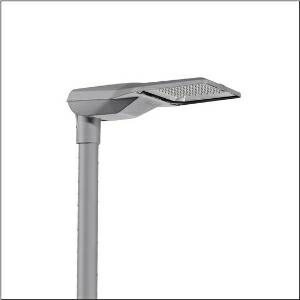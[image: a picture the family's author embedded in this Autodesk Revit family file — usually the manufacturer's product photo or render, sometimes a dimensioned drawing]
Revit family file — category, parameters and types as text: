
# Revit family: streetlight_sl_21_iq_midi___pl52_5xe3h41g08mb_9f92
name_source: partatom
category: Lighting Fixtures
units: mm (PartAtom-declared; Revit-internal decimal feet)

## family parameters
Cut with Voids When Loaded = No
Host = Face
Light Source = No
Part Type = Normal
Room Calculation Point = No
Round Connector Dimension = Use Diameter
Shared = No

## types (1)
- --- (1 x LED, 20000 lm, 146.7 W, 4000K)
    Apparent Load = 147 VA
    CIE Flux Codes = 27 59 98 100 100
    Color Rendering = 70
    Color Temperature = 4000K
    Default Elevation = 1800 mm
    Description = Streetlight SL 21 iQ midi, mast luminaire, primary light control with lens, of PMMA, primary optical cover: cover, of toughened safety glass, transparent, light distribution: PL52, light emission: direct distribution, primary light characteristic: asymmetric, installation type: post-top, side-entry, LED, High Power LED, rated luminous flux: 20.000lm, luminous efficacy: 136lm/W, light colour: 740, colour temperature: 4000K, control gear: iQ Street-Remote, control: Street-Remote, Auto-Match, Temp-Guard, Lumen-Switch, Night-Set, Smart-Wire, Light-Fading, Desk-Remote (wireless, voltage-free reading and setting of iQ features in the workshop via application-optimized NFC function/RFID function), optimised constant luminous flux control (CLO 2.0), pre-setting: linear dimming characteristic, mains connection: 230..240V, AC, 50/60Hz, start of lifetime: 147W, end of service life: 161W, reduction: 62W, luminaire housing, of diecast aluminium, powder-coated, Siteco® metallic grey (DB 702S), corrosivity category C5 mid according to DIN EN ISO 12944, please order mast flange separately, inclination adjustable: 0°, 5°, 10°, 15°, sealing non-destructively replaceable, multi-level sealing system, length: 644mm, width: 335mm, height: 110mm, mast flange for spigot size: 42mm (side-entry): 5XC10008XM4, 60/48mm (side-entry/post-top): 5XC10108XM2, 76/60mm (side-entry/post-top): 5XC10108XM1, mounting height: 4..8m, protection rating (complete): IP66, insulation class (complete): insulation class II (safety insulation), certification: CE, ENEC, ENEC+, VDE, impact resistance: IK10, permissible operating ambient temperature for outdoor applications: -40..+50°C, standard-compliant lighting for roads and squares, packaging unit: 1 piece

Light Distribution: PL52
    Height = 111 mm
    Lamp = 1 x LED
    Lamp Light Flux = 20000 lm
    Lamp Power = 146.7 W
    Lamp count = 1
    Length = 644 mm
    Luminous efficacy = 136 lm/W
    Manufacturer = Siteco
    ModVariant = No
    Model = 5XE3H41G08MB
    Number of Poles = 1
    OnlyDefault = Yes
    Power Factor = 1
    Product Name = Streetlight SL 21 iQ midi | PL52
    Product group = mast luminaire | pylon top
    ProductGroupID = 6100
    Protection Class = Protection class II
    Protection Degree = IP 66
    RLX_Detail_Level = 1
    RLX_Emergency_Light_Flux = 0 lm
    RLX_Emergency_Type = 0
    RLX_Emergency_Type_DB = No
    RlxData = <blob elided: 36625 chars, md5=75058d87>
    Socket = socket
    Standby Power = 0 W
    System Light Flux = 20000 lm
    System Power = 147 W
    Type Comments = factory setting: luminous flux: 100 % | dim-lin: 254 | 753 mA
    Type Image = l_1004298.jpg
    URL = http://relux.com
    VarID = @adj_212003
    Voltage = 0 V
    Weight = 0.00 kg
    Width = 336 mm

## geometry (parser evidence)
native form markers: Blend x4, Sweep x12
no freeform markers — native parametric forms only
